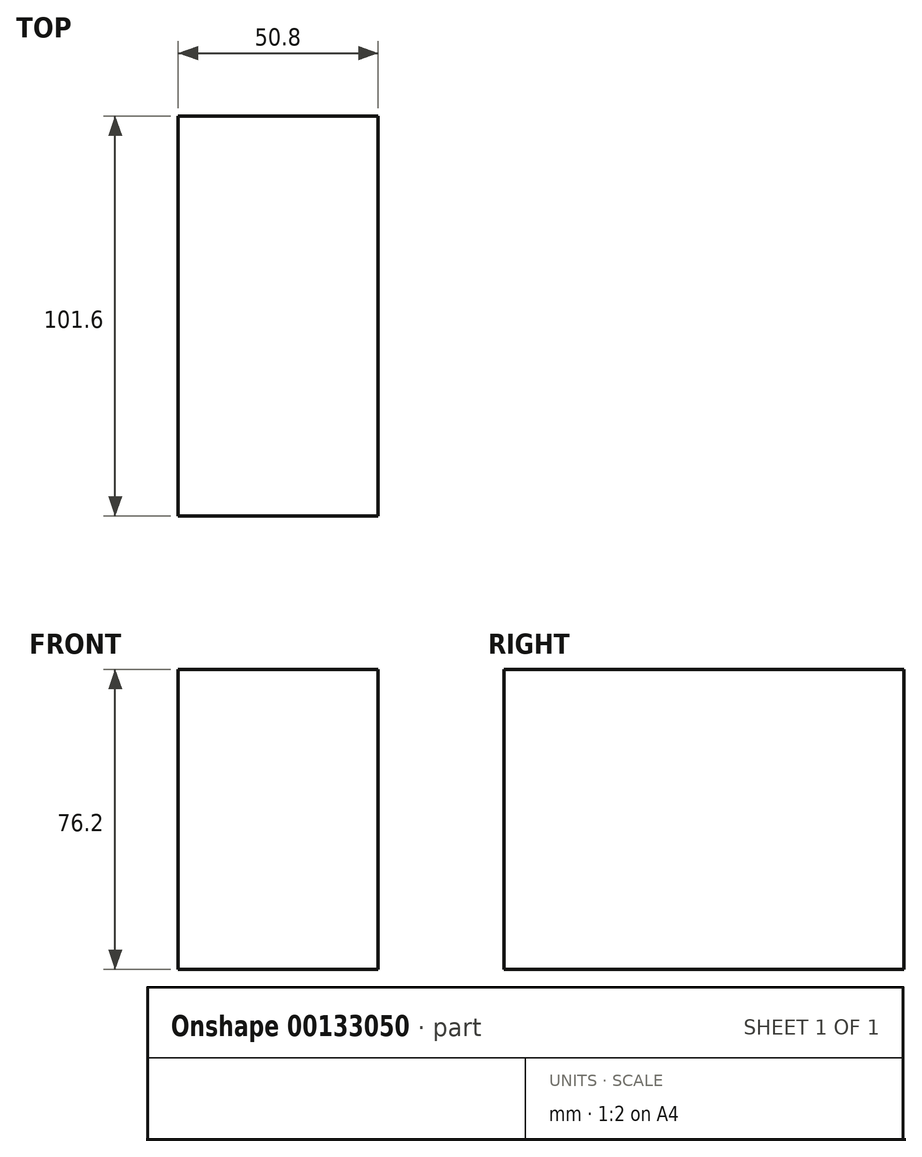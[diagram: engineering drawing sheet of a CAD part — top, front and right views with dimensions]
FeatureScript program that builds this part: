
annotation { "Feature Type Name" : "Feature", "Feature Type Description" : "" }
export const myFeature = defineFeature(function(context is Context, id is Id, definition is map)
    precondition{}
    {
        {
            var Q0;
            Q0=qCreatedBy(makeId("Front.planeOp"),FACE);
            var sketch = newSketch(context, id + "F0", { "sketchPlane" : qUnion([Q0])});
            skLineSegment(sketch, "E0.bottom", {"start": v(-23.66, 62.88) * mm, "end": v(27.14, 62.88) * mm});
            skLineSegment(sketch, "E0.top", {"start": v(-23.66, -13.32) * mm, "end": v(27.14, -13.32) * mm});
            skLineSegment(sketch, "E0.left", {"start": v(-23.66, 62.88) * mm, "end": v(-23.66, -13.32) * mm});
            skLineSegment(sketch, "E0.right", {"start": v(27.14, 62.88) * mm, "end": v(27.14, -13.32) * mm});
            skSolve(sketch);
        }
        {
            var Q0;
            Q0 = qSketchRegion(id + "F0", true);
            extrude(context, id + "F1", {"entities" : qUnion([Q0]), "depth" : 101.6 * mm});
        }
    });
